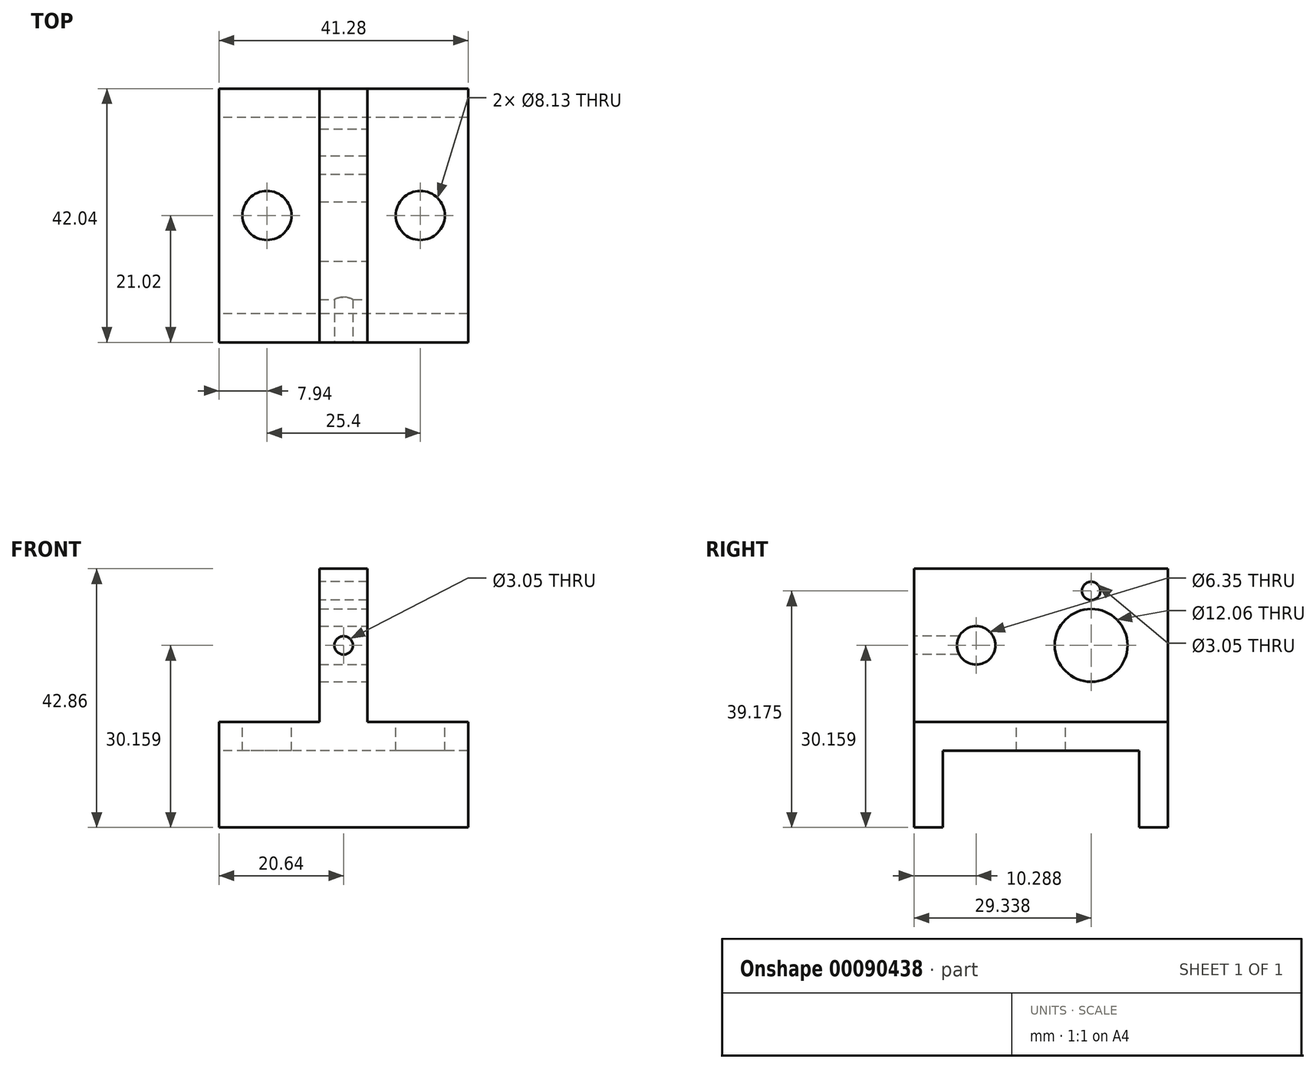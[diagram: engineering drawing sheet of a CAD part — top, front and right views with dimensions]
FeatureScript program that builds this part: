
annotation { "Feature Type Name" : "Feature", "Feature Type Description" : "" }
export const myFeature = defineFeature(function(context is Context, id is Id, definition is map)
    precondition{}
    {
        {
            var Q0;
            Q0=qCreatedBy(makeId("Right.planeOp"),FACE);
            var sketch = newSketch(context, id + "F0", { "sketchPlane" : qUnion([Q0])});
            skLineSegment(sketch, "E0.bottom", {"start": v(-16.26, 16.26) * mm, "end": v(16.26, 16.26) * mm});
            skLineSegment(sketch, "E0.top", {"start": v(-16.26, -16.26) * mm, "end": v(16.26, -16.26) * mm, "construction": true});
            skLineSegment(sketch, "E0.left", {"start": v(-16.26, 16.26) * mm, "end": v(-16.26, 3.56) * mm});
            skLineSegment(sketch, "E0.right", {"start": v(16.26, 16.26) * mm, "end": v(16.26, 3.56) * mm});
            skPoint(sketch, "E0.middle", {"position": v(0, 0) * mm});
            skLineSegment(sketch, "E1", {"start": v(-16.26, 3.56) * mm, "end": v(-21.02, 3.56) * mm});
            skLineSegment(sketch, "E2", {"start": v(-21.02, 3.56) * mm, "end": v(-21.02, 21.02) * mm});
            skLineSegment(sketch, "E3", {"start": v(-21.02, 21.02) * mm, "end": v(21.02, 21.02) * mm});
            skLineSegment(sketch, "E4", {"start": v(21.02, 21.02) * mm, "end": v(21.02, 3.56) * mm});
            skLineSegment(sketch, "E5", {"start": v(21.02, 3.56) * mm, "end": v(16.26, 3.56) * mm});
            skLineSegment(sketch, "E6", {"start": v(16.26, 16.26) * mm, "end": v(16.26, 21.02) * mm, "construction": true});
            skLineSegment(sketch, "E7", {"start": v(-16.26, 3.56) * mm, "end": v(-16.26, -16.26) * mm, "construction": true});
            skLineSegment(sketch, "E8", {"start": v(16.26, 3.56) * mm, "end": v(16.26, -16.26) * mm, "construction": true});
            skLineSegment(sketch, "E9", {"start": v(0, 16.26) * mm, "end": v(0, -16.26) * mm, "construction": true});
            skSolve(sketch);
        }
        {
            var Q0;
            Q0 = qSketchRegion(id + "F0", true);
            extrude(context, id + "F1", {"entities" : qUnion([Q0]), "endBound" : BoundingType.SYMMETRIC, "depth" : 41.27 * mm});
        }
        {
            var Q0;
            Q0=makeQuery(id+"F1.opExtrude","SWEPT_FACE",FACE,{"disambiguationData":[OSD([sQuery(id+"F0.wireOp",EDGE,"E3")])]});
            var sketch = newSketch(context, id + "F2", { "sketchPlane" : qUnion([Q0])});
            skCircle(sketch, "E10", {"center": v(-12.7, 0) * mm, "radius": 4.06 * mm});
            skCircle(sketch, "E11", {"center": v(12.7, 0) * mm, "radius": 4.06 * mm});
            skLineSegment(sketch, "E12", {"start": v(-12.7, 0) * mm, "end": v(0, 0) * mm, "construction": true});
            skLineSegment(sketch, "E13", {"start": v(0, 0) * mm, "end": v(12.7, 0) * mm, "construction": true});
            skSolve(sketch);
        }
        {
            var Q0;
            Q0 = qSketchRegion(id + "F2", true);
            extrude(context, id + "F3", {"entities" : qUnion([Q0]), "operationType" : NewBodyOperationType.REMOVE, "endBound" : BoundingType.UP_TO_NEXT, "oppositeDirection" : true, "depth" : 25.4 * mm});
        }
        {
            var Q0;
            Q0=makeQuery(id+"F1.opExtrude","SWEPT_FACE",FACE,{"disambiguationData":[OSD([sQuery(id+"F0.wireOp",EDGE,"E3")])]});
            var sketch = newSketch(context, id + "F4", { "sketchPlane" : qUnion([Q0])});
            skLineSegment(sketch, "E14.bottom", {"start": v(-3.97, 21.02) * mm, "end": v(3.97, 21.02) * mm});
            skLineSegment(sketch, "E14.top", {"start": v(-3.97, -21.02) * mm, "end": v(3.97, -21.02) * mm});
            skLineSegment(sketch, "E14.left", {"start": v(-3.97, 21.02) * mm, "end": v(-3.97, -21.02) * mm});
            skLineSegment(sketch, "E14.right", {"start": v(3.97, 21.02) * mm, "end": v(3.97, -21.02) * mm});
            skPoint(sketch, "E14.middle", {"position": v(0, 0) * mm});
            skSolve(sketch);
        }
        {
            var Q0;
            Q0 = qSketchRegion(id + "F4", true);
            extrude(context, id + "F5", {"entities" : qUnion([Q0]), "operationType" : NewBodyOperationType.ADD, "depth" : 25.4 * mm});
        }
        {
            var Q0;
            Q0=makeQuery(id+"F5.opExtrude","SWEPT_FACE",FACE,{"disambiguationData":[OSD([sQuery(id+"F4.wireOp",EDGE,"E14.right")])]});
            var sketch = newSketch(context, id + "F6", { "sketchPlane" : qUnion([Q0])});
            skCircle(sketch, "E15", {"center": v(8.32, 33.72) * mm, "radius": 6.03 * mm});
            skLineSegment(sketch, "E16", {"start": v(21.02, 33.72) * mm, "end": v(8.32, 33.72) * mm, "construction": true});
            skCircle(sketch, "E17", {"center": v(-10.73, 33.72) * mm, "radius": 3.18 * mm});
            skLineSegment(sketch, "E18", {"start": v(-10.73, 33.72) * mm, "end": v(-21.02, 33.72) * mm, "construction": true});
            skSolve(sketch);
        }
        {
            var Q0;
            Q0 = qSketchRegion(id + "F6", true);
            extrude(context, id + "F7", {"entities" : qUnion([Q0]), "operationType" : NewBodyOperationType.REMOVE, "endBound" : BoundingType.UP_TO_NEXT, "oppositeDirection" : true, "depth" : 25.4 * mm});
        }
        {
            var Q0;
            Q0=makeQuery(id+"F5.opExtrude","SWEPT_FACE",FACE,{"disambiguationData":[OSD([sQuery(id+"F4.wireOp",EDGE,"E14.left")])]});
            var sketch = newSketch(context, id + "F8", { "sketchPlane" : qUnion([Q0])});
            skCircle(sketch, "E19", {"center": v(-8.32, 33.72) * mm, "radius": 6.86 * mm, "construction": true});
            skCircle(sketch, "E20", {"center": v(-8.32, 42.74) * mm, "radius": 1.52 * mm});
            skLineSegment(sketch, "E21", {"start": v(-8.32, 40.58) * mm, "end": v(-8.32, 33.72) * mm, "construction": true});
            skLineSegment(sketch, "E22", {"start": v(-8.32, 40.58) * mm, "end": v(-8.32, 41.21) * mm, "construction": true});
            skLineSegment(sketch, "E23", {"start": v(-8.32, 41.21) * mm, "end": v(-8.32, 42.74) * mm, "construction": true});
            skSolve(sketch);
        }
        {
            var Q0;
            Q0 = qSketchRegion(id + "F8", true);
            extrude(context, id + "F9", {"entities" : qUnion([Q0]), "operationType" : NewBodyOperationType.REMOVE, "endBound" : BoundingType.UP_TO_NEXT, "oppositeDirection" : true, "depth" : 25.4 * mm});
        }
        {
            var Q0;
            Q0=makeQuery(id+"F5.boolean.opBoolean","MERGE",FACE,{"derivedFrom":[makeQuery(id+"F1.opExtrude","SWEPT_FACE",FACE,{"disambiguationData":[OSD([sQuery(id+"F0.wireOp",EDGE,"E2")])]}),makeQuery(id+"F5.opExtrude","SWEPT_FACE",FACE,{"disambiguationData":[OSD([sQuery(id+"F4.wireOp",EDGE,"E14.top")])]})]});
            var sketch = newSketch(context, id + "F10", { "sketchPlane" : qUnion([Q0])});
            skLineSegment(sketch, "E24.0", {"start": v(3.97, 36.9) * mm, "end": v(3.97, 30.54) * mm, "construction": true});
            skLineSegment(sketch, "E25", {"start": v(3.97, 33.72) * mm, "end": v(-3.97, 33.72) * mm, "construction": true});
            skCircle(sketch, "E26", {"center": v(0, 33.72) * mm, "radius": 1.52 * mm});
            skSolve(sketch);
        }
        {
            var Q0;
            Q0 = qSketchRegion(id + "F10", true);
            extrude(context, id + "F11", {"entities" : qUnion([Q0]), "operationType" : NewBodyOperationType.REMOVE, "endBound" : BoundingType.UP_TO_NEXT, "oppositeDirection" : true, "depth" : 25.4 * mm});
        }
    });
